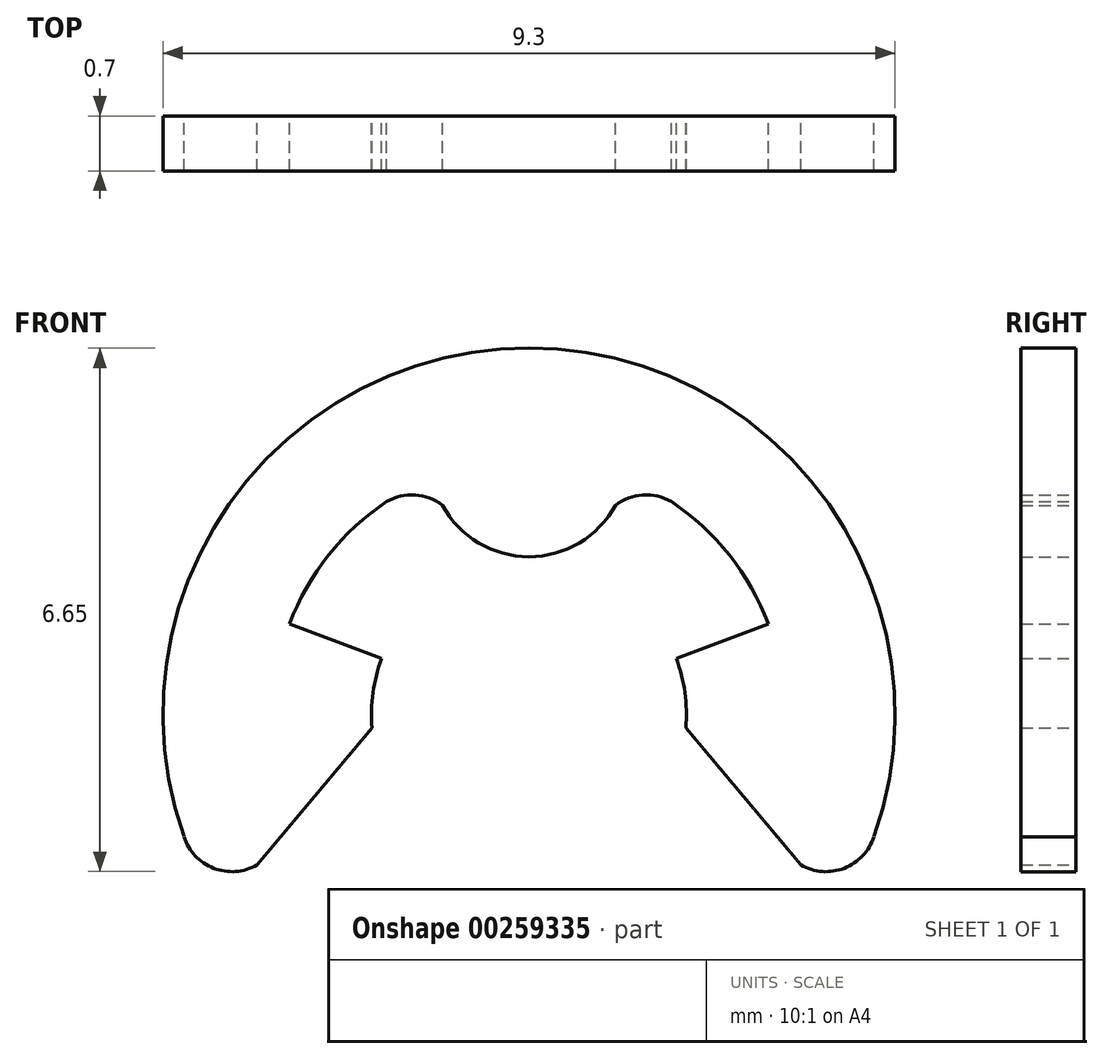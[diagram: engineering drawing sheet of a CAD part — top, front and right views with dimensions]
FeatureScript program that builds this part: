
annotation { "Feature Type Name" : "Feature", "Feature Type Description" : "" }
export const myFeature = defineFeature(function(context is Context, id is Id, definition is map)
    precondition{}
    {
        {
            var Q0;
            Q0=qCreatedBy(makeId("Front.planeOp"),FACE);
            var sketch = newSketch(context, id + "F0", { "sketchPlane" : qUnion([Q0])});
            skArc(sketch, "E0", {"start": v(4.37, -1.6) * mm, "mid": v(0, 4.65) * mm, "end": v(-4.37, -1.6) * mm});
            skArc(sketch, "E1", {"start": v(-1.8, 2.7) * mm, "mid": v(-2.55, 2.02) * mm, "end": v(-3.04, 1.15) * mm});
            skArc(sketch, "E2", {"start": v(-1.1, 2.65) * mm, "mid": v(0, 2) * mm, "end": v(1.1, 2.65) * mm});
            skArc(sketch, "E3", {"start": v(1.9, 2.64) * mm, "mid": v(1.5, 2.79) * mm, "end": v(1.1, 2.65) * mm});
            skArc(sketch, "E4.MirrorCS", {"start": v(-1.9, 2.64) * mm, "mid": v(-1.5, 2.79) * mm, "end": v(-1.1, 2.65) * mm});
            skLineSegment(sketch, "E5", {"start": v(1.87, 0.7) * mm, "end": v(3.04, 1.15) * mm});
            skLineSegment(sketch, "E6", {"start": v(2, -0.17) * mm, "end": v(3.46, -1.92) * mm});
            skArc(sketch, "E7.trimOffspring", {"start": v(3.04, 1.15) * mm, "mid": v(2.55, 2.02) * mm, "end": v(1.8, 2.7) * mm});
            skArc(sketch, "E8", {"start": v(3.46, -1.92) * mm, "mid": v(4, -1.96) * mm, "end": v(4.38, -1.56) * mm});
            skLineSegment(sketch, "E9.MirrorCS", {"start": v(-1.87, 0.7) * mm, "end": v(-3.04, 1.15) * mm});
            skLineSegment(sketch, "E10.MirrorCS", {"start": v(-2, -0.17) * mm, "end": v(-3.46, -1.92) * mm});
            skArc(sketch, "E11.MirrorCS", {"start": v(-3.46, -1.92) * mm, "mid": v(-4, -1.96) * mm, "end": v(-4.38, -1.56) * mm});
            skArc(sketch, "E12", {"start": v(-1.87, 0.7) * mm, "mid": v(-1.98, 0.27) * mm, "end": v(-2, -0.17) * mm});
            skArc(sketch, "E13.MirrorCS", {"start": v(1.87, 0.7) * mm, "mid": v(1.98, 0.27) * mm, "end": v(2, -0.17) * mm});
            skSolve(sketch);
        }
        {
            var Q0;
            Q0 = qSketchRegion(id + "F0", true);
            extrude(context, id + "F1", {"entities" : qUnion([Q0]), "endBound" : BoundingType.SYMMETRIC, "depth" : 0.7 * mm});
        }
    });
